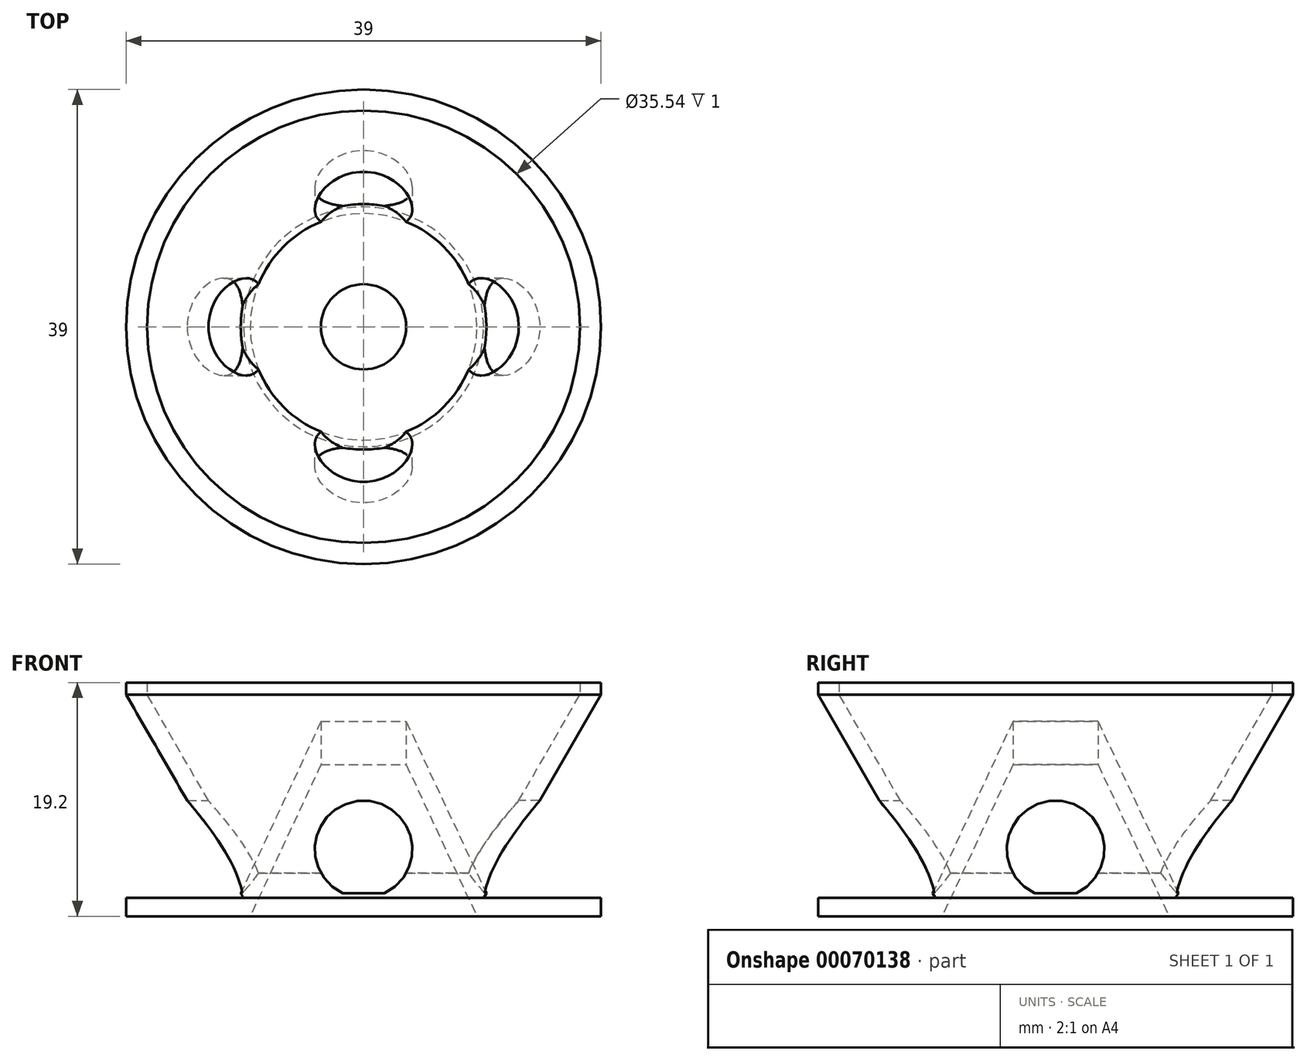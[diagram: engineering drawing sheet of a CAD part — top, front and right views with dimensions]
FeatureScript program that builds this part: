
annotation { "Feature Type Name" : "Feature", "Feature Type Description" : "" }
export const myFeature = defineFeature(function(context is Context, id is Id, definition is map)
    precondition{}
    {
        {
            var Q0;
            Q0=qCreatedBy(makeId("Front.planeOp"),FACE);
            var sketch = newSketch(context, id + "F0", { "sketchPlane" : qUnion([Q0])});
            skLineSegment(sketch, "E0", {"start": v(0, 0) * mm, "end": v(0, 26.58) * mm, "construction": true});
            skLineSegment(sketch, "E1", {"start": v(-9.3, 0) * mm, "end": v(-19.5, 0) * mm});
            skLineSegment(sketch, "E2", {"start": v(-19.5, 0) * mm, "end": v(-19.5, 1.5) * mm});
            skLineSegment(sketch, "E3", {"start": v(-19.5, 1.5) * mm, "end": v(-9.86, 1.5) * mm});
            skLineSegment(sketch, "E4", {"start": v(-3.5, 16) * mm, "end": v(-3.5, 12.46) * mm});
            skLineSegment(sketch, "E5", {"start": v(-3.5, 12.46) * mm, "end": v(-9.3, 0) * mm});
            skLineSegment(sketch, "E6", {"start": v(-3.5, 16) * mm, "end": v(-9.3, 3.55) * mm});
            skLineSegment(sketch, "E7", {"start": v(-9.3, 3.55) * mm, "end": v(-17.77, 18.2) * mm});
            skLineSegment(sketch, "E8", {"start": v(-19.5, 18.2) * mm, "end": v(-9.86, 1.5) * mm});
            skLineSegment(sketch, "E9", {"start": v(-19.5, 18.2) * mm, "end": v(-17.77, 18.2) * mm});
            skSolve(sketch);
        }
        {
            var Q0;
            Q0 = qSketchRegion(id + "F0", true);
            var Q1;
            Q1=sQuery(id+"F0.wireOp",EDGE,"E0");
            revolve(context, id + "F1", {"entities" : qUnion([Q0]), "axis" : qUnion([Q1]), "revolveType" : RevolveType.FULL});
        }
        {
            var Q0;
            Q0=qCreatedBy(makeId("Right.planeOp"),FACE);
            cPlane(context, id + "F2", {"entities" : qUnion([Q0]), "cplaneType" : CPlaneType.OFFSET, "offset" : 11 * mm, "width" : 150 * mm, "height" : 150 * mm});
        }
        {
            var Q0;
            Q0=qCreatedBy(id+"F2.planeOp",FACE);
            var sketch = newSketch(context, id + "F3", { "sketchPlane" : qUnion([Q0])});
            skCircle(sketch, "E10", {"center": v(0, 5.5) * mm, "radius": 4 * mm});
            skSolve(sketch);
        }
        {
            var Q0;
            Q0 = qSketchRegion(id + "F3", true);
            var Q1;
            Q1=makeQuery(id+"F1.opRevolve","SWEPT_FACE",FACE,{"disambiguationData":[OSD([sQuery(id+"F0.wireOp",EDGE,"E6")])]});
            extrude(context, id + "F4", {"entities" : qUnion([Q0]), "operationType" : NewBodyOperationType.REMOVE, "endBound" : BoundingType.THROUGH_ALL, "depth" : 1.6 * mm, "hasSecondDirection" : true, "secondDirectionBound" : SecondDirectionBoundingType.UP_TO_SURFACE, "secondDirectionOppositeDirection" : true, "secondDirectionBoundEntityFace" : qUnion([Q1]), "secondDirectionDepth" : 25 * mm});
        }
        {
            var Q0;
            Q0=makeQuery(id+"F1.opRevolve","SWEPT_BODY",BODY,{"disambiguationData":[OSD([sQuery(id+"F0.wireOp",EDGE,"E1"),sQuery(id+"F0.wireOp",EDGE,"E2"),sQuery(id+"F0.wireOp",EDGE,"E3"),sQuery(id+"F0.wireOp",EDGE,"E4"),sQuery(id+"F0.wireOp",EDGE,"E5"),sQuery(id+"F0.wireOp",EDGE,"E6"),sQuery(id+"F0.wireOp",EDGE,"E7"),sQuery(id+"F0.wireOp",EDGE,"E8"),sQuery(id+"F0.wireOp",EDGE,"E9")])]});
            var Q1;
            Q1=qCreatedBy(makeId("Right.planeOp"),FACE);
            mirror(context, id + "F5", {"operationType" : NewBodyOperationType.INTERSECT, "entities" : qUnion([Q0]), "mirrorPlane" : qUnion([Q1])});
        }
        {
            var Q0;
            Q0=qCreatedBy(makeId("Front.planeOp"),FACE);
            cPlane(context, id + "F6", {"entities" : qUnion([Q0]), "cplaneType" : CPlaneType.OFFSET, "offset" : 11 * mm, "width" : 150 * mm, "height" : 150 * mm});
        }
        {
            var Q0;
            Q0=qCreatedBy(id+"F6.planeOp",FACE);
            var sketch = newSketch(context, id + "F7", { "sketchPlane" : qUnion([Q0])});
            skCircle(sketch, "E11", {"center": v(0, 5.5) * mm, "radius": 4 * mm});
            skLineSegment(sketch, "E12", {"start": v(0, 9.5) * mm, "end": v(0, 1.5) * mm, "construction": true});
            skSolve(sketch);
        }
        {
            var Q0;
            Q0 = qSketchRegion(id + "F7", true);
            var Q1;
            {var subQ0=makeQuery(id+"F4.boolean.opBoolean","MERGE",FACE,{"derivedFrom":[makeQuery(id+"F1.opRevolve","SWEPT_FACE",FACE,{"disambiguationData":[OSD([sQuery(id+"F0.wireOp",EDGE,"E6")])]}),makeQuery(id+"F4.opExtrude","CAP_FACE",FACE,{"disambiguationData":[OSD([sQuery(id+"F3.wireOp",EDGE,"E10")]),OD(0.0)],"isStart":false})]});Q1=makeQuery(id+"F5.boolean.opBoolean","MERGE",FACE,{"derivedFrom":[subQ0,makeQuery(id+"F5.boolean.toolComplement.opBoolean","COPY",FACE,{"derivedFrom":makeQuery(id+"F5.opPattern","COPY",FACE,{"derivedFrom":subQ0,"instanceName":"1"})})]});}
            extrude(context, id + "F8", {"entities" : qUnion([Q0]), "operationType" : NewBodyOperationType.REMOVE, "endBound" : BoundingType.THROUGH_ALL, "depth" : 25 * mm, "hasSecondDirection" : true, "secondDirectionBound" : SecondDirectionBoundingType.UP_TO_SURFACE, "secondDirectionOppositeDirection" : true, "secondDirectionBoundEntityFace" : qUnion([Q1]), "secondDirectionDepth" : 25 * mm});
        }
        {
            var Q0;
            Q0=makeQuery(id+"F1.opRevolve","SWEPT_BODY",BODY,{"disambiguationData":[OSD([sQuery(id+"F0.wireOp",EDGE,"E1"),sQuery(id+"F0.wireOp",EDGE,"E2"),sQuery(id+"F0.wireOp",EDGE,"E3"),sQuery(id+"F0.wireOp",EDGE,"E4"),sQuery(id+"F0.wireOp",EDGE,"E5"),sQuery(id+"F0.wireOp",EDGE,"E6"),sQuery(id+"F0.wireOp",EDGE,"E7"),sQuery(id+"F0.wireOp",EDGE,"E8"),sQuery(id+"F0.wireOp",EDGE,"E9")])]});
            var Q1;
            Q1=qCreatedBy(makeId("Front.planeOp"),FACE);
            mirror(context, id + "F9", {"operationType" : NewBodyOperationType.INTERSECT, "entities" : qUnion([Q0]), "mirrorPlane" : qUnion([Q1])});
        }
        {
            var Q0;
            Q0=makeQuery(id+"F1.opRevolve","SWEPT_FACE",FACE,{"disambiguationData":[OSD([sQuery(id+"F0.wireOp",EDGE,"E9")])]});
            var sketch = newSketch(context, id + "F10", { "sketchPlane" : qUnion([Q0])});
            skCircle(sketch, "E13", {"center": v(0, 0) * mm, "radius": 17.77 * mm});
            skCircle(sketch, "E14", {"center": v(0, 0) * mm, "radius": 19.5 * mm});
            skSolve(sketch);
        }
        {
            var Q0;
            Q0 = qSketchRegion(id + "F10", true);
            extrude(context, id + "F11", {"entities" : qUnion([Q0]), "operationType" : NewBodyOperationType.ADD, "depth" : 1 * mm});
        }
    });
